# Revit family: 1450xx Aquina Ceiling 360 (UL)
name_source: partatom
category: Lighting Fixtures
units: mm (PartAtom-declared; Revit-internal decimal feet)

## family parameters
Always vertical = Yes
Cut with Voids When Loaded = No
Host = Ceiling
Light Source = No
Maintain Annotation Orientation = No
OmniClass Number = 23.80.70.11
OmniClass Title = Luminaries for Internal Lighting
Part Type = Normal
Room Calculation Point = No
Round Connector Dimension = Use Diameter
Shared = No

## types (2) — shared parameters
Dimmable = Yes
Dimming Method = Lamp Dependent
Driver Included = Not Applicable
Driver Required = No
Efficacy (lm/w) = Lamp Dependent (lm/W)
Lamp = LED
Main Finish = Various
Main Material = Metal - Mild Steel
Manufacturer URL - Europe and Rest of World = www.astrolighting.com
Manufacturer URL - North America = us.astrolighting.com
Power (Watts) = Lamp Dependent
Product Dimensions (MM) = 176 x 360
Product Location = Bathroom Indoor
Product Weight (KG) = 5 mm  [stored 0.0164042 ft]
zero-valued in all types: Default Elevation

## per-type parameters (varying)
| type | ADA compliant | Electrical Class | Length of supplied cable | Location / IP Rating | Product Name | Product SKU |
| CE | Not Applicable | CE (Class 1) |  | IP44 | Aquina Ceiling 360 | 1450004 |
| ETL | Yes - if installed in compliance with ADA §307.4 | 1 | Not Applicable | Not Applicable | Aquina Ceiling 360 (UL) | 1450008 |

note: [stored X ft] marks values corroborated as IEEE doubles in the binary element streams (Revit-internal decimal feet)

## geometry (parser evidence)
native form markers: Sweep x3
no freeform markers — native parametric forms only
